# Revit family: Steni - Profile - Horizontal Joint HP 7-30
name_source: partatom
category: Generic Models
revit_build: Autodesk Revit Architecture 2016 (Build: 20151007_0715(x64)
units: mm (PartAtom-declared; Revit-internal decimal feet)

## family parameters
Always vertical = Yes
Can host rebar = No
Cut with Voids When Loaded = No
Part Type = Normal
Room Calculation Point = No
Round Connector Dimension = Use Diameter
Shared = No
Work Plane-Based = No

## types (3) — shared parameters
DepthBig = 5 mm  [stored 0.0164042 ft]
DepthSmall = 1 mm  [stored 0.00328084 ft]
Description = Aluminium profile for Steni facade systems
Manufacturer = www.steni.com
Material main = Steni Aluminium Profile Black RAL9005
Model = HP 7-30
Product family = Steni Profiles
URL = http://bimobject.com
zero-valued in all types: Width

## type names (no varying parameters)
- Anodized 15µ
- S 0502-Y White
- RAL 9005 Black

note: [stored X ft] marks values corroborated as IEEE doubles in the binary element streams (Revit-internal decimal feet)

## geometry (parser evidence)
native form markers: Blend x4, Sweep x2
no freeform markers — native parametric forms only
